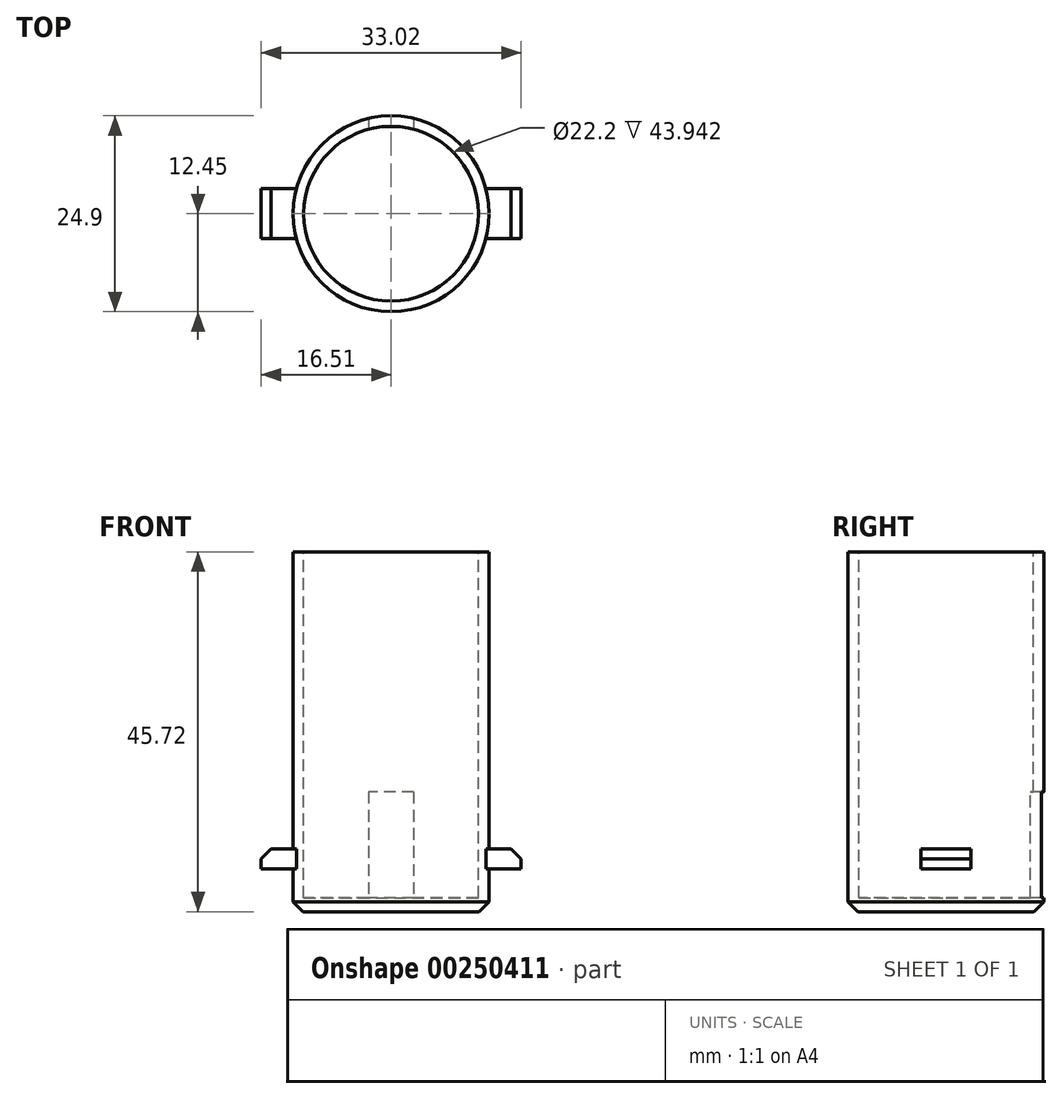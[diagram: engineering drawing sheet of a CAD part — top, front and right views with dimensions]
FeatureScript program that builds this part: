
annotation { "Feature Type Name" : "Feature", "Feature Type Description" : "" }
export const myFeature = defineFeature(function(context is Context, id is Id, definition is map)
    precondition{}
    {
        {
            var Q0;
            Q0=qCreatedBy(makeId("Top.planeOp"),FACE);
            var sketch = newSketch(context, id + "F0", { "sketchPlane" : qUnion([Q0])});
            skCircle(sketch, "E0", {"center": v(0, 0) * mm, "radius": 12.45 * mm});
            skSolve(sketch);
        }
        {
            var Q0;
            Q0 = qSketchRegion(id + "F0", true);
            extrude(context, id + "F1", {"entities" : qUnion([Q0]), "depth" : 45.72 * mm});
        }
        {
            var Q0;
            Q0=qCreatedBy(makeId("Top.planeOp"),FACE);
            cPlane(context, id + "F2", {"entities" : qUnion([Q0]), "cplaneType" : CPlaneType.OFFSET, "offset" : 5.46 * mm, "width" : 152.4 * mm, "height" : 152.4 * mm});
        }
        {
            var Q0;
            Q0=qCreatedBy(id+"F2.planeOp",FACE);
            var sketch = newSketch(context, id + "F3", { "sketchPlane" : qUnion([Q0])});
            skLineSegment(sketch, "E1", {"start": v(-17.12, 0) * mm, "end": v(25.27, 0) * mm, "construction": true});
            skLineSegment(sketch, "E2.bottom", {"start": v(16.51, 3.17) * mm, "end": v(-16.51, 3.17) * mm});
            skLineSegment(sketch, "E2.top", {"start": v(16.51, -3.18) * mm, "end": v(-16.51, -3.18) * mm});
            skLineSegment(sketch, "E2.left", {"start": v(16.51, 3.18) * mm, "end": v(16.51, -3.18) * mm});
            skLineSegment(sketch, "E2.right", {"start": v(-16.51, 3.18) * mm, "end": v(-16.51, -3.18) * mm});
            skPoint(sketch, "E2.middle", {"position": v(0, 0) * mm});
            skSolve(sketch);
        }
        {
            var Q0;
            Q0 = qSketchRegion(id + "F3", true);
            extrude(context, id + "F4", {"entities" : qUnion([Q0]), "operationType" : NewBodyOperationType.ADD, "depth" : 2.54 * mm});
        }
        {
            var Q0;
            Q0=makeQuery(id+"F1.opExtrude","CAP_FACE",FACE,{"disambiguationData":[OSD([sQuery(id+"F0.wireOp",EDGE,"E0")])],"isStart":false});
            var sketch = newSketch(context, id + "F5", { "sketchPlane" : qUnion([Q0])});
            skCircle(sketch, "E3", {"center": v(0, 0) * mm, "radius": 11.1 * mm});
            skSolve(sketch);
        }
        {
            var Q0;
            Q0 = qSketchRegion(id + "F5", true);
            extrude(context, id + "F6", {"entities" : qUnion([Q0]), "operationType" : NewBodyOperationType.REMOVE, "oppositeDirection" : true, "depth" : 43.94 * mm});
        }
        {
            var Q0;
            Q0=qCreatedBy(makeId("Front.planeOp"),FACE);
            var sketch = newSketch(context, id + "F7", { "sketchPlane" : qUnion([Q0])});
            skLineSegment(sketch, "E4.bottom", {"start": v(2.87, 15.24) * mm, "end": v(-2.87, 15.24) * mm});
            skLineSegment(sketch, "E4.top", {"start": v(2.87, 1.78) * mm, "end": v(-2.87, 1.78) * mm});
            skLineSegment(sketch, "E4.left", {"start": v(2.87, 15.24) * mm, "end": v(2.87, 1.78) * mm});
            skLineSegment(sketch, "E4.right", {"start": v(-2.87, 15.24) * mm, "end": v(-2.87, 1.78) * mm});
            skPoint(sketch, "E4.middle", {"position": v(0, 8.5) * mm});
            skSolve(sketch);
        }
        {
            var Q0;
            Q0 = qSketchRegion(id + "F7", true);
            extrude(context, id + "F8", {"entities" : qUnion([Q0]), "operationType" : NewBodyOperationType.REMOVE, "oppositeDirection" : true, "depth" : 25.4 * mm});
        }
        {
            var Q0;
            Q0=makeQuery(id+"F1.opExtrude","CAP_EDGE",EDGE,{"disambiguationData":[OSD([sQuery(id+"F0.wireOp",EDGE,"E0")])],"isStart":true});
            var Q1;
            Q1=makeQuery(id+"F4.opExtrude","CAP_EDGE",EDGE,{"disambiguationData":[OSD([sQuery(id+"F3.wireOp",EDGE,"E2.right")])],"isStart":false});
            var Q2;
            Q2=makeQuery(id+"F4.opExtrude","CAP_EDGE",EDGE,{"disambiguationData":[OSD([sQuery(id+"F3.wireOp",EDGE,"E2.left")])],"isStart":false});
            var Q3;
            Q3=makeQuery(id+"F6.boolean.opBoolean","COPY",EDGE,{"derivedFrom":makeQuery(id+"F6.opExtrude","CAP_EDGE",EDGE,{"disambiguationData":[OSD([sQuery(id+"F5.wireOp",EDGE,"E3")])],"isStart":true})});
            chamfer(context, id + "F9", {"entities" : qUnion([Q0, Q1, Q2, Q3]), "width" : 1.27 * mm, "tangentPropagation" : true});
        }
    });
